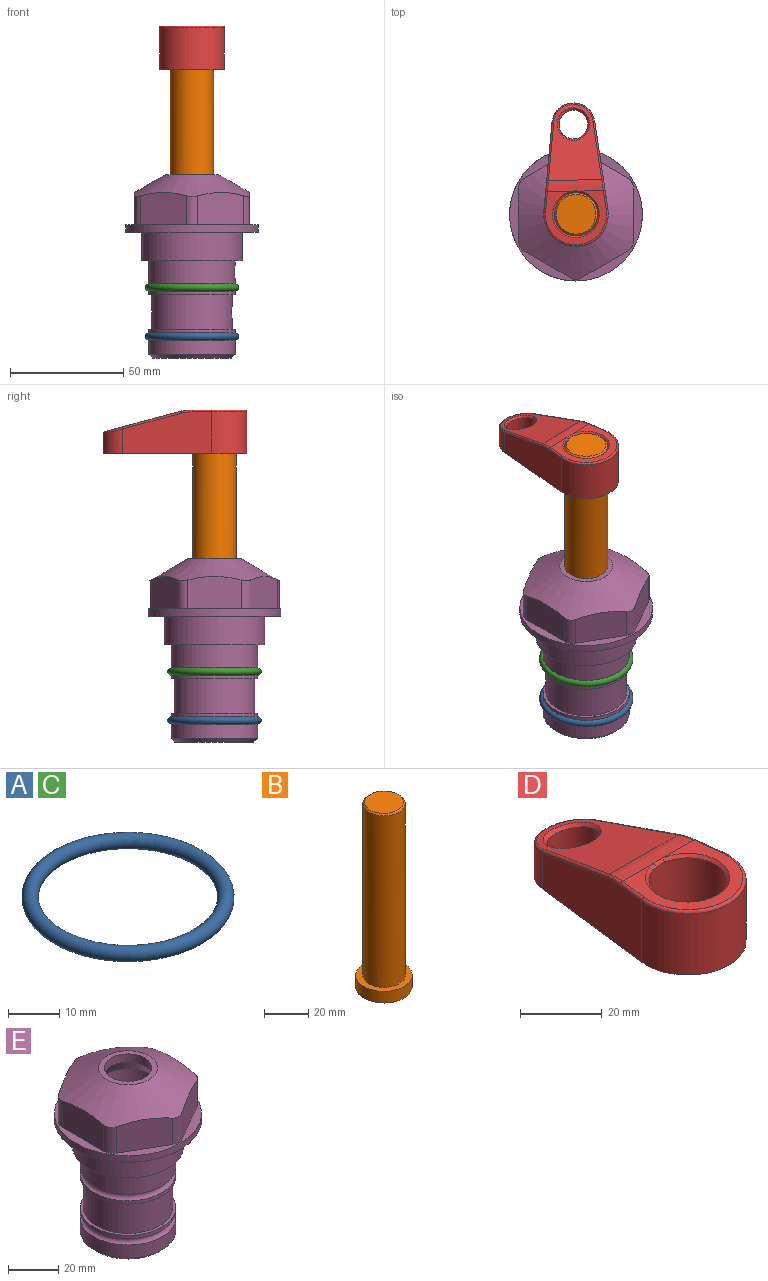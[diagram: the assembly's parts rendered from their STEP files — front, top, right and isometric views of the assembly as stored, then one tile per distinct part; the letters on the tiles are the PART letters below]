
ASSEMBLY  parts=5 mates=4
PART A: 1 faces, bbox 44.7x44.7x3.2 mm
  f0: torus R=19.05mm, axis (0,0,1), area 1193.9mm2
PART B: 6 faces, bbox 25.4x25.4x101.6 mm
  f0: plane 17.46x17.46mm, normal (0,0,1), area 239.5mm2, adj f5
  f1: plane 25.4x25.4mm, normal (0,0,-1), area 506.7mm2, adj f2
  f2: cylinder r=12.7mm len=25.4mm, axis (0,0,1), area 506.7mm2, adj f1,f3
  f3: plane 25.4x25.4mm, normal (0,0,1), area 221.7mm2, adj f2,f4
  f4: cylinder r=9.53mm len=94.46mm, axis (0,0,1), area 5653mm2, adj f3,f5
  f5: cone r=8.73mm half-angle=45deg, axis (0,0,-1), area 64.4mm2, adj f0,f4
PART C: same geometry as A
PART D: 31 faces, bbox 31.7x65.5x19.8 mm
  f0: plane 39.12x18.26mm, normal (0.99,0.12,0), area 612.2mm2, adj f1,f4,f7,f11,f13,f15
  f1: cylinder r=9.53mm len=18.91mm, axis (0,0,-1), area 296.1mm2, adj f0,f2,f7,f17
  f2: plane 39.12x18.26mm, normal (-0.99,0.12,0), area 612.2mm2, adj f1,f4,f7,f12,f14,f16
  f3: cylinder r=6.35mm len=12.7mm, axis (0,0,-1), area 362.4mm2, adj f7,f18
  f4: cylinder r=14.29mm len=28.58mm, axis (0,0,-1), area 882.2mm2, adj f0,f2,f7,f10
  f5: cylinder r=9.53mm len=19.05mm, axis (0,0,-1), area 1092.6mm2, adj f7,f19,f20
  f6: plane 26.99x23.69mm, normal (0,0,1), area 216.2mm2, adj f9,f10,f11,f12,f19
  f7: plane 63.5x28.58mm, normal (0,0,-1), area 661.8mm2, adj f0,f1,f2,f3,f4,f5,f22,f23
  f8: plane 33.52x23.6mm, normal (0,0.26,0.97), area 486mm2, adj f9,f15,f16,f17,f18
  f9: cylinder r=19.05mm len=24.72mm, axis (1,0,0), area 120.4mm2, adj f6,f8,f13,f14,f20
  f10: torus R=13.49mm, axis (0,0,1), area 59mm2, adj f4,f6,f11,f12
  f11: cylinder r=0.79mm len=8.67mm, axis (0.12,-0.99,0), area 10.8mm2, adj f0,f6,f10,f13
  f12: cylinder r=0.79mm len=8.67mm, axis (0.12,0.99,0), area 10.8mm2, adj f2,f6,f10,f14
  f13: bspline ~4.95x1.42mm, area 6.1mm2, adj f0,f9,f11,f15
  f14: bspline ~4.95x1.42mm, area 6.1mm2, adj f2,f9,f12,f16
  f15: cylinder r=0.79mm len=25.95mm, axis (0.12,-0.96,0.26), area 32.9mm2, adj f0,f8,f13,f17
  f16: cylinder r=0.79mm len=25.95mm, axis (0.12,0.96,-0.26), area 32.9mm2, adj f2,f8,f14,f17
  f17: bspline ~18.91x8.38mm, area 30mm2, adj f1,f8,f15,f16
  f18: bspline ~14.29x14.29mm, area 48.3mm2, adj f3,f8
  f19: cone r=9.53mm half-angle=45deg, axis (0,0,1), area 66.5mm2, adj f5,f6,f20
  f20: bspline ~3.22x0.96mm, area 3.5mm2, adj f5,f9,f19
  f21: plane 2.75x2.72mm, normal (0,0,-1), area 2.9mm2, adj f23,f25,f28
  f22: plane 23.05x15.88mm, normal (-0.99,-0.12,0), area 323.6mm2, adj f7,f25,f26,f27,f28,f29
  f23: plane 23.05x15.88mm, normal (0.99,-0.12,0), area 323.6mm2, adj f7,f21,f25,f27,f28,f30
  f24: cylinder r=9.53mm len=10.69mm, axis (0,0,-1), area 114.7mm2, adj f7,f27,f29,f30
  f25: cylinder r=12.7mm len=20.59mm, axis (0,0,-1), area 381.1mm2, adj f7,f21,f22,f23,f26,f28
  f26: plane 2.75x2.72mm, normal (0,0,-1), area 2.9mm2, adj f22,f25,f28
  f27: plane 19.72x18.37mm, normal (0,-0.26,-0.97), area 291.8mm2, adj f22,f23,f24,f28,f29,f30
  f28: cylinder r=15.88mm len=19.92mm, axis (1,0,0), area 54.8mm2, adj f21,f22,f23,f25,f26,f27
  f29: cylinder r=1.59mm len=11mm, axis (0,0,-1), area 34.7mm2, adj f7,f22,f24,f27
  f30: cylinder r=1.59mm len=11mm, axis (0,0,-1), area 34.7mm2, adj f7,f23,f24,f27
PART E: 36 faces, bbox 58.7x58.7x81 mm
  f0: cylinder r=17.78mm len=35.56mm, axis (0,0,1), area 1670.8mm2, adj f23,f24,f31
  f1: cylinder r=19.05mm len=38.1mm, axis (0,0,1), area 1191.9mm2, adj f26,f27,f30
  f2: plane 58.66x58.66mm, normal (0,0,-1), area 1150.6mm2, adj f3,f28
  f3: cylinder r=29.33mm len=58.66mm, axis (0,0,-1), area 585.1mm2, adj f2,f4
  f4: plane 58.66x58.66mm, normal (0,0,1), area 475.9mm2, adj f3,f5,f6,f7,f8,f9,f10,f11
  f5: plane 20.32x14.34mm, normal (-0.5,0.87,0), area 324.4mm2, adj f4,f15,f16,f17
  f6: plane 20.32x14.34mm, normal (0.5,0.87,0), area 324.4mm2, adj f4,f14,f15,f17
  f7: plane 23.48x14.34mm, normal (1,0,0), area 324.4mm2, adj f4,f13,f14,f17
  f8: plane 20.32x14.34mm, normal (0.5,-0.87,0), area 324.4mm2, adj f4,f12,f13,f17
  f9: plane 20.32x14.34mm, normal (-0.5,-0.87,0), area 324.4mm2, adj f4,f11,f12,f17
  f10: plane 23.48x14.34mm, normal (-1,0,0), area 324.4mm2, adj f4,f11,f16,f17
  f11: cylinder r=5.08mm len=12.85mm, axis (0,0,-1), area 67.2mm2, adj f4,f9,f10,f17
  f12: cylinder r=5.08mm len=12.85mm, axis (0,0,-1), area 67.2mm2, adj f4,f8,f9,f17
  f13: cylinder r=5.08mm len=12.85mm, axis (0,0,-1), area 67.2mm2, adj f4,f7,f8,f17
  f14: cylinder r=5.08mm len=12.85mm, axis (0,0,-1), area 67.2mm2, adj f4,f6,f7,f17
  f15: cylinder r=5.08mm len=12.85mm, axis (0,0,-1), area 67.2mm2, adj f4,f5,f6,f17
  f16: cylinder r=5.08mm len=12.85mm, axis (0,0,-1), area 67.2mm2, adj f4,f5,f10,f17
  f17: cone r=11.73mm half-angle=60deg, axis (0,0,-1), area 2071.8mm2, adj f5,f6,f7,f8,f9,f10,f11,f12
  f18: plane 23.46x23.46mm, normal (0,0,1), area 147.4mm2, adj f17,f35
  f19: plane 34.93x34.93mm, normal (0,0,-1), area 958mm2, adj f29
  f20: cylinder r=19.05mm len=38.1mm, axis (0,0,1), area 760.1mm2, adj f21,f29
  f21: torus R=19.05mm, axis (0,0,1), area 565.3mm2, adj f20,f22
  f22: cylinder r=19.05mm len=38.1mm, axis (0,0,1), area 190mm2, adj f21,f23
  f23: plane 38.1x38.1mm, normal (0,0,1), area 146.9mm2, adj f0,f22
  f24: plane 38.1x38.1mm, normal (0,0,-1), area 146.9mm2, adj f0,f25
  f25: cylinder r=19.05mm len=38.1mm, axis (0,0,1), area 190mm2, adj f24,f26
  f26: torus R=19.05mm, axis (0,0,1), area 565.3mm2, adj f1,f25
  f27: plane 44.45x44.45mm, normal (0,0,-1), area 411.7mm2, adj f1,f28
  f28: cylinder r=22.23mm len=44.45mm, axis (0,0,1), area 1773.5mm2, adj f2,f27
  f29: cone r=19.05mm half-angle=45deg, axis (0,0,1), area 257.5mm2, adj f19,f20
  f30: cylinder r=3.17mm len=6.75mm, axis (-1,0,0), area 128mm2, adj f1,f33
  f31: cylinder r=3.17mm len=6.35mm, axis (-1,0,0), area 102.5mm2, adj f0,f33
  f32: plane 25.4x25.4mm, normal (0,0,1), area 506.7mm2, adj f33
  f33: cylinder r=12.7mm len=66.42mm, axis (0,0,-1), area 5236.2mm2, adj f30,f31,f32,f34
  f34: cone r=9.53mm half-angle=30deg, axis (0,0,-1), area 443.4mm2, adj f33,f35
  f35: cylinder r=9.53mm len=19.05mm, axis (0,0,-1), area 240.9mm2, adj f18,f34
PLACE A t=(0,0,-21.59)mm
PLACE B rot(axis=(0,0,1),1.6deg) t=(0,0,27.55)mm
PLACE C at identity
PLACE D rot(axis=(0,0,1),1.6deg) t=(0,0,27.55)mm
PLACE E at identity fixed
MATE fastened C.f0 <-> E.f0  axis (0,0,1) through (0,0,-24.51)mm
MATE cylindrical B.f2 <-> E.f0  axis (0,0,-1) through (0,0,-10.55)mm
MATE fastened A.f0 <-> E.f0  axis (0,0,1) through (0,0,-46.1)mm
MATE fastened D.f4 <-> B.f2  axis (0,0,1) through (0,0,91.05)mm
